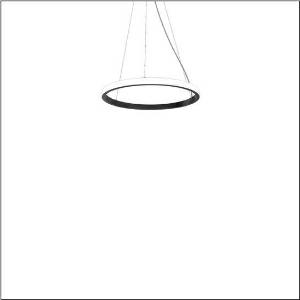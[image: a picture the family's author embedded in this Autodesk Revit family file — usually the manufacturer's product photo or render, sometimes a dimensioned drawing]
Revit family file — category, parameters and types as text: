
# Revit family: silica_21_ring-o_5pjbo1d3104a
name_source: partatom
category: Lighting Fixtures
units: mm (PartAtom-declared; Revit-internal decimal feet)

## family parameters
Cut with Voids When Loaded = No
Host = Face
Light Source = No
Part Type = Normal
Room Calculation Point = No
Round Connector Dimension = Use Diameter
Shared = No

## types (1)
- Silica 21 Ring-O (1 x LED, 3930 lm, 60 W, 4000K)
    Apparent Load = 60 VA
    CIE Flux Codes = 2 16 49 50 100
    Color Rendering = 80
    Color Temperature = 4000K
    Default Elevation = 1800 mm
    Description = Silica 21 Ring-O, suspended luminaire, of PMMA, frosted, light emission: outer ring side luminous distribution, primary light characteristic: symmetric, installation type: suspended mounting, LED, rated luminous flux: 3.930lm, luminous efficacy: 66lm/W, light colour: 840, colour temperature: 4000K, control gear: DALI 2, with terminal, 5-pole, mains connection: 230V, AC/DC, 0/50..60Hz, rated input power: 60W, housing, of extruded aluminium section, jet black (RAL 9005), diameter: 610mm, ceiling canopy, jet black (RAL 9005), protection rating (lamp compartment): IP40, insulation class (complete): insulation class I (protective earthing), certification: CE, impact resistance: IK02, permissible operating ambient temperature: 0..+35°C, packaging unit: 1 piece
    Height = 48 mm  [stored 0.15748 ft]
    Lamp = 1 x LED
    Lamp Light Flux = 3930 lm
    Lamp Power = 60 W
    Lamp count = 1
    Length = 610 mm
    Luminous efficacy = 66 lm/W
    Manufacturer = Siteco
    ModVariant = No
    Model = 5PJBO1D3104A
    Mounting Place = Ceiling
    Mounting Type = Pendant
    Number of Poles = 1
    OnlyDefault = Yes
    Power Factor = 1
    Product Name = Silica 21 Ring-O
    Product group = suspended luminaire
    ProductGroupID = 904
    Protection Class = Protection class I
    Protection Degree = IP 40
    RLX_Detail_Level = 1
    RLX_Emergency_Light_Flux = 0 lm
    RLX_Emergency_Type = 0
    RLX_Emergency_Type_DB = No
    RlxData = <blob elided: 12157 chars, md5=129e32da>
    Socket = socket
    Standby Power = 0 W
    System Light Flux = 3930 lm
    System Power = 60 W
    Type Comments = Product without accessories
    Type Image = l_1258377.jpg
    URL = http://relux.com
    VarID = ---
    Voltage = 0 V
    Weight = 0.00 kg
    Width = 0 mm  [stored 0 ft]

note: [stored X ft] marks values corroborated as IEEE doubles in the binary element streams (Revit-internal decimal feet)

## geometry (parser evidence)
native form markers: Sweep x12
no freeform markers — native parametric forms only
